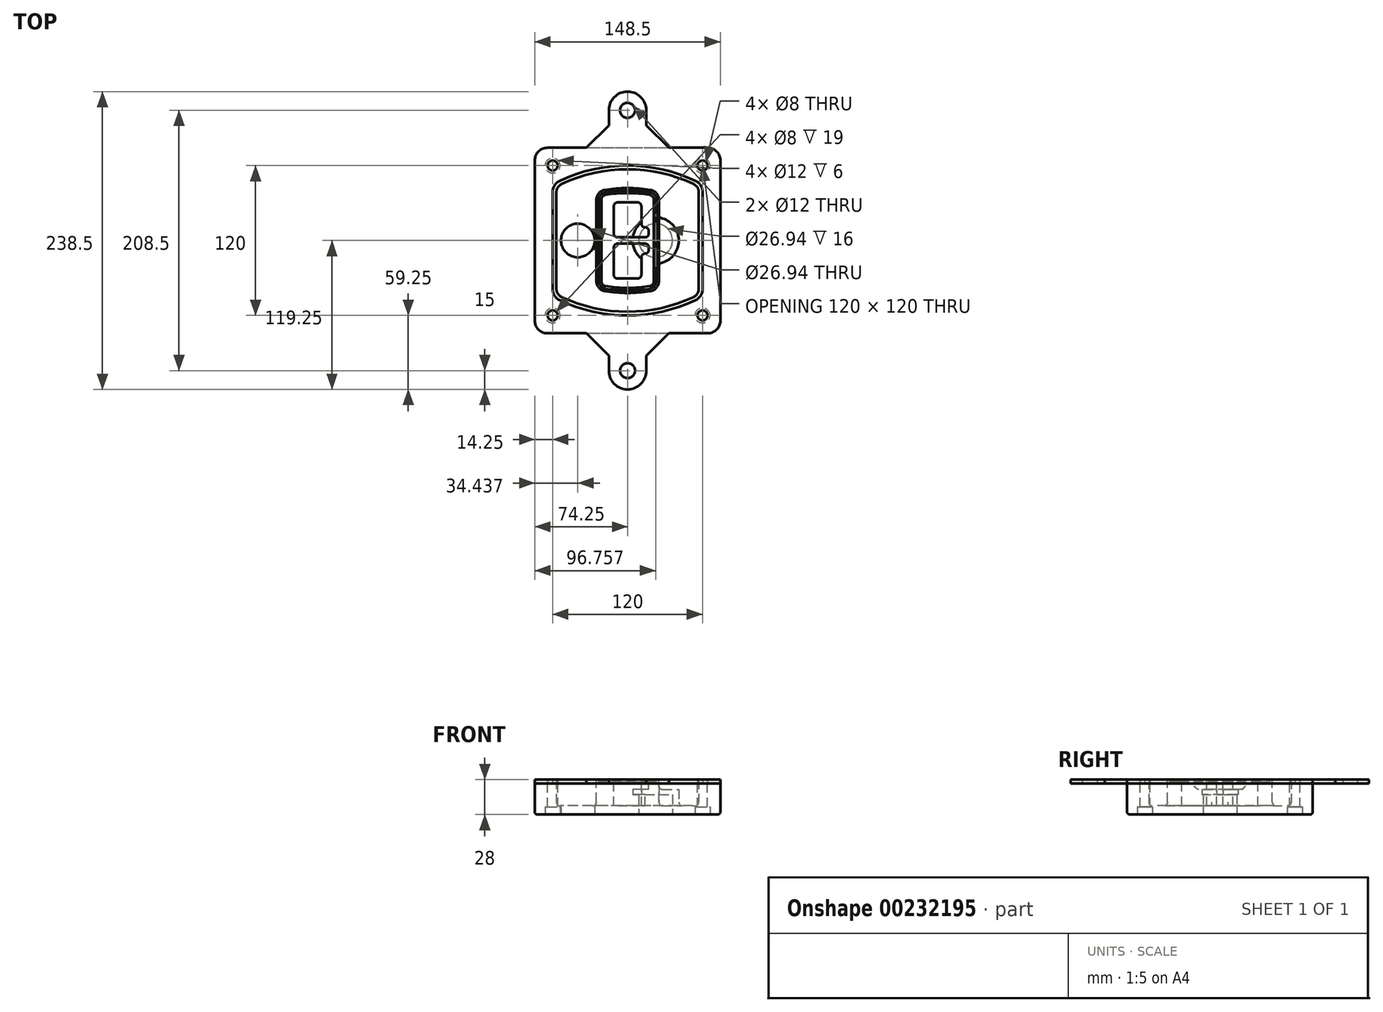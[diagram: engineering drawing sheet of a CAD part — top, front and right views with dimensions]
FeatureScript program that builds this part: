
annotation { "Feature Type Name" : "Feature", "Feature Type Description" : "" }
export const myFeature = defineFeature(function(context is Context, id is Id, definition is map)
    precondition{}
    {
        {
            var Q0;
            Q0=qCreatedBy(makeId("Top.planeOp"),FACE);
            var sketch = newSketch(context, id + "F0", { "sketchPlane" : qUnion([Q0])});
            skPoint(sketch, "E0.rect.middle", {"position": v(0, 0) * mm});
            skLineSegment(sketch, "E1.bottom", {"start": v(-64.25, -74.25) * mm, "end": v(64.25, -74.25) * mm});
            skLineSegment(sketch, "E1.top", {"start": v(-64.25, 74.25) * mm, "end": v(64.25, 74.25) * mm});
            skLineSegment(sketch, "E1.left", {"start": v(-74.25, -64.25) * mm, "end": v(-74.25, 64.25) * mm});
            skLineSegment(sketch, "E1.right", {"start": v(74.25, -64.25) * mm, "end": v(74.25, 64.25) * mm});
            skLineSegment(sketch, "E2", {"start": v(-74.25, 74.25) * mm, "end": v(74.25, -74.25) * mm, "construction": true});
            skLineSegment(sketch, "E3", {"start": v(74.25, 74.25) * mm, "end": v(-74.25, -74.25) * mm, "construction": true});
            skCircle(sketch, "E4", {"center": v(-60, 60) * mm, "radius": 4 * mm});
            skCircle(sketch, "E5", {"center": v(60, 60) * mm, "radius": 4 * mm});
            skCircle(sketch, "E6", {"center": v(60, -60) * mm, "radius": 4 * mm});
            skCircle(sketch, "E7", {"center": v(-60, -60) * mm, "radius": 4 * mm});
            skLineSegment(sketch, "E8", {"start": v(-60, 60) * mm, "end": v(60, 60) * mm, "construction": true});
            skLineSegment(sketch, "E9", {"start": v(60, 60) * mm, "end": v(60, -60) * mm, "construction": true});
            skLineSegment(sketch, "E10", {"start": v(60, -60) * mm, "end": v(-60, -60) * mm, "construction": true});
            skLineSegment(sketch, "E11", {"start": v(-60, -60) * mm, "end": v(-60, 60) * mm, "construction": true});
            skLineSegment(sketch, "E12", {"start": v(-60, 38.83) * mm, "end": v(-60, -38.83) * mm});
            skLineSegment(sketch, "E13", {"start": v(60, 38.83) * mm, "end": v(60, -38.83) * mm});
            skArc(sketch, "E14", {"start": v(54.26, 47.88) * mm, "mid": v(0, 60) * mm, "end": v(-54.26, 47.88) * mm});
            skArc(sketch, "E15", {"start": v(-54.26, -47.88) * mm, "mid": v(0, -60) * mm, "end": v(54.26, -47.88) * mm});
            skLineSegment(sketch, "E16", {"start": v(-60, 0) * mm, "end": v(60, 0) * mm, "construction": true});
            skPoint(sketch, "E17.visualSharp", {"position": v(-60, -45) * mm});
            skArc(sketch, "E17.filletArc", {"start": v(-60, -38.83) * mm, "mid": v(-58.44, -44.2) * mm, "end": v(-54.26, -47.88) * mm});
            skPoint(sketch, "E18.visualSharp", {"position": v(-60, 45) * mm});
            skArc(sketch, "E18.filletArc", {"start": v(-54.26, 47.88) * mm, "mid": v(-58.44, 44.2) * mm, "end": v(-60, 38.83) * mm});
            skPoint(sketch, "E19.visualSharp", {"position": v(60, 45) * mm});
            skArc(sketch, "E19.filletArc", {"start": v(60, 38.83) * mm, "mid": v(58.44, 44.2) * mm, "end": v(54.26, 47.88) * mm});
            skPoint(sketch, "E20.visualSharp", {"position": v(60, -45) * mm});
            skArc(sketch, "E20.filletArc", {"start": v(54.26, -47.88) * mm, "mid": v(58.44, -44.2) * mm, "end": v(60, -38.83) * mm});
            skPoint(sketch, "E21.visualSharp", {"position": v(-74.25, 74.25) * mm});
            skArc(sketch, "E21.filletArc", {"start": v(-64.25, 74.25) * mm, "mid": v(-71.32, 71.32) * mm, "end": v(-74.25, 64.25) * mm});
            skPoint(sketch, "E22.visualSharp", {"position": v(74.25, 74.25) * mm});
            skArc(sketch, "E22.filletArc", {"start": v(74.25, 64.25) * mm, "mid": v(71.32, 71.32) * mm, "end": v(64.25, 74.25) * mm});
            skPoint(sketch, "E23.visualSharp", {"position": v(74.25, -74.25) * mm});
            skArc(sketch, "E23.filletArc", {"start": v(64.25, -74.25) * mm, "mid": v(71.32, -71.32) * mm, "end": v(74.25, -64.25) * mm});
            skPoint(sketch, "E24.visualSharp", {"position": v(-74.25, -74.25) * mm});
            skArc(sketch, "E24.filletArc", {"start": v(-74.25, -64.25) * mm, "mid": v(-71.32, -71.32) * mm, "end": v(-64.25, -74.25) * mm});
            skArc(sketch, "E25.0", {"start": v(57, 38.83) * mm, "mid": v(55.9, 42.58) * mm, "end": v(52.98, 45.17) * mm});
            skLineSegment(sketch, "E25.1", {"start": v(57, 38.83) * mm, "end": v(57, -38.83) * mm});
            skArc(sketch, "E25.2", {"start": v(52.98, -45.17) * mm, "mid": v(55.9, -42.58) * mm, "end": v(57, -38.83) * mm});
            skArc(sketch, "E25.3", {"start": v(-52.98, -45.17) * mm, "mid": v(0, -57) * mm, "end": v(52.98, -45.17) * mm});
            skArc(sketch, "E25.4", {"start": v(-57, -38.83) * mm, "mid": v(-55.9, -42.58) * mm, "end": v(-52.98, -45.17) * mm});
            skArc(sketch, "E25.5", {"start": v(52.98, 45.17) * mm, "mid": v(0, 57) * mm, "end": v(-52.98, 45.17) * mm});
            skLineSegment(sketch, "E25.6", {"start": v(-57, 38.83) * mm, "end": v(-57, -38.83) * mm});
            skArc(sketch, "E25.7", {"start": v(-52.98, 45.17) * mm, "mid": v(-55.9, 42.58) * mm, "end": v(-57, 38.83) * mm});
            skArc(sketch, "E26.0", {"start": v(-55.96, 51.5) * mm, "mid": v(-61.82, 46.33) * mm, "end": v(-64, 38.83) * mm});
            skArc(sketch, "E26.1", {"start": v(55.96, 51.5) * mm, "mid": v(0, 64) * mm, "end": v(-55.96, 51.5) * mm});
            skArc(sketch, "E26.2", {"start": v(64, 38.83) * mm, "mid": v(61.82, 46.33) * mm, "end": v(55.96, 51.5) * mm});
            skLineSegment(sketch, "E26.3", {"start": v(64, 38.83) * mm, "end": v(64, -38.83) * mm});
            skArc(sketch, "E26.4", {"start": v(55.96, -51.5) * mm, "mid": v(61.82, -46.33) * mm, "end": v(64, -38.83) * mm});
            skLineSegment(sketch, "E26.5", {"start": v(-64, 38.83) * mm, "end": v(-64, -38.83) * mm});
            skArc(sketch, "E26.6", {"start": v(-55.96, -51.5) * mm, "mid": v(0, -64) * mm, "end": v(55.96, -51.5) * mm});
            skArc(sketch, "E26.7", {"start": v(-64, -38.83) * mm, "mid": v(-61.82, -46.33) * mm, "end": v(-55.96, -51.5) * mm});
            skSolve(sketch);
        }
        {
            var Q0;
            Q0=makeQuery(id+"F0.imprint","IMPRINT",FACE,{"disambiguationData":[TD([[makeQuery(id+"F0.imprint","IMPRINT",EDGE,{"derivedFrom":sQuery(id+"F0.wireOp",EDGE,"E1.bottom")}),1.0]])]});
            var Q1;
            Q1=makeQuery(id+"F0.imprint","IMPRINT",FACE,{"disambiguationData":[TD([[makeQuery(id+"F0.imprint","IMPRINT",EDGE,{"derivedFrom":sQuery(id+"F0.wireOp",EDGE,"E12")}),1.0]])]});
            var Q2;
            Q2=makeQuery(id+"F0.imprint","IMPRINT",FACE,{"disambiguationData":[TD([[makeQuery(id+"F0.imprint","IMPRINT",EDGE,{"derivedFrom":sQuery(id+"F0.wireOp",EDGE,"E25.0")}),1.0]])]});
            var Q3;
            Q3=makeQuery(id+"F0.imprint","IMPRINT",FACE,{"disambiguationData":[TD([[makeQuery(id+"F0.imprint","IMPRINT",EDGE,{"derivedFrom":sQuery(id+"F0.wireOp",EDGE,"E12")}),-1.0]])]});
            extrude(context, id + "F1", {"entities" : qUnion([Q0, Q1, Q2, Q3]), "oppositeDirection" : true, "depth" : 25 * mm});
        }
        {
            var Q0;
            Q0=makeQuery(id+"F0.imprint","IMPRINT",FACE,{"disambiguationData":[TD([[makeQuery(id+"F0.imprint","IMPRINT",EDGE,{"derivedFrom":sQuery(id+"F0.wireOp",EDGE,"E12")}),1.0]])]});
            extrude(context, id + "F2", {"entities" : qUnion([Q0]), "operationType" : NewBodyOperationType.ADD, "depth" : 3 * mm});
        }
        {
            var Q0;
            Q0=makeQuery(id+"F0.imprint","IMPRINT",FACE,{"disambiguationData":[TD([[makeQuery(id+"F0.imprint","IMPRINT",EDGE,{"derivedFrom":sQuery(id+"F0.wireOp",EDGE,"E25.0")}),1.0]])]});
            extrude(context, id + "F3", {"entities" : qUnion([Q0]), "operationType" : NewBodyOperationType.REMOVE, "oppositeDirection" : true, "depth" : 18 * mm});
        }
        {
            var Q0;
            Q0=makeQuery(id+"F2.opExtrude","CAP_FACE",FACE,{"disambiguationData":[OSD([sQuery(id+"F0.wireOp",EDGE,"E12"),sQuery(id+"F0.wireOp",EDGE,"E13"),sQuery(id+"F0.wireOp",EDGE,"E14"),sQuery(id+"F0.wireOp",EDGE,"E15"),sQuery(id+"F0.wireOp",EDGE,"E17.filletArc"),sQuery(id+"F0.wireOp",EDGE,"E18.filletArc"),sQuery(id+"F0.wireOp",EDGE,"E19.filletArc"),sQuery(id+"F0.wireOp",EDGE,"E20.filletArc"),sQuery(id+"F0.wireOp",EDGE,"E25.0"),sQuery(id+"F0.wireOp",EDGE,"E25.1"),sQuery(id+"F0.wireOp",EDGE,"E25.2"),sQuery(id+"F0.wireOp",EDGE,"E25.3"),sQuery(id+"F0.wireOp",EDGE,"E25.4"),sQuery(id+"F0.wireOp",EDGE,"E25.5"),sQuery(id+"F0.wireOp",EDGE,"E25.6"),sQuery(id+"F0.wireOp",EDGE,"E25.7")])],"isStart":false});
            var sketch = newSketch(context, id + "F4", { "sketchPlane" : qUnion([Q0])});
            skArc(sketch, "E27.0", {"start": v(-18.34, -40.45) * mm, "mid": v(0, -42) * mm, "end": v(18.34, -40.45) * mm});
            skArc(sketch, "E28.0", {"start": v(18.34, 40.45) * mm, "mid": v(0, 42) * mm, "end": v(-18.34, 40.45) * mm});
            skLineSegment(sketch, "E29", {"start": v(-25, 32.57) * mm, "end": v(-25, -32.57) * mm});
            skLineSegment(sketch, "E30", {"start": v(25, 32.57) * mm, "end": v(25, -32.57) * mm});
            skLineSegment(sketch, "E31", {"start": v(-25, 39.1) * mm, "end": v(25, 39.1) * mm, "construction": true});
            skLineSegment(sketch, "E32", {"start": v(-25, -39.1) * mm, "end": v(25, -39.1) * mm, "construction": true});
            skPoint(sketch, "E33.visualSharp", {"position": v(-25, 39.1) * mm});
            skArc(sketch, "E33.filletArc", {"start": v(-18.34, 40.45) * mm, "mid": v(-23.11, 37.73) * mm, "end": v(-25, 32.57) * mm});
            skPoint(sketch, "E34.visualSharp", {"position": v(25, 39.1) * mm});
            skArc(sketch, "E34.filletArc", {"start": v(25, 32.57) * mm, "mid": v(23.11, 37.73) * mm, "end": v(18.34, 40.45) * mm});
            skPoint(sketch, "E35.visualSharp", {"position": v(25, -39.1) * mm});
            skArc(sketch, "E35.filletArc", {"start": v(18.34, -40.45) * mm, "mid": v(23.11, -37.73) * mm, "end": v(25, -32.57) * mm});
            skPoint(sketch, "E36.visualSharp", {"position": v(-25, -39.1) * mm});
            skArc(sketch, "E36.filletArc", {"start": v(-25, -32.57) * mm, "mid": v(-23.11, -37.73) * mm, "end": v(-18.34, -40.45) * mm});
            skArc(sketch, "E37.0", {"start": v(52.98, 45.17) * mm, "mid": v(0, 57) * mm, "end": v(-52.98, 45.17) * mm});
            skArc(sketch, "E37.1", {"start": v(-52.98, 45.17) * mm, "mid": v(-55.9, 42.58) * mm, "end": v(-57, 38.83) * mm});
            skLineSegment(sketch, "E37.2", {"start": v(-57, 38.83) * mm, "end": v(-57, -38.83) * mm});
            skArc(sketch, "E37.3", {"start": v(-57, -38.83) * mm, "mid": v(-55.9, -42.58) * mm, "end": v(-52.98, -45.17) * mm});
            skArc(sketch, "E37.4", {"start": v(-52.98, -45.17) * mm, "mid": v(0, -57) * mm, "end": v(52.98, -45.17) * mm});
            skArc(sketch, "E37.5", {"start": v(52.98, -45.17) * mm, "mid": v(55.9, -42.58) * mm, "end": v(57, -38.83) * mm});
            skLineSegment(sketch, "E37.6", {"start": v(57, 38.83) * mm, "end": v(57, -38.83) * mm});
            skArc(sketch, "E37.7", {"start": v(57, 38.83) * mm, "mid": v(55.9, 42.58) * mm, "end": v(52.98, 45.17) * mm});
            skLineSegment(sketch, "E38.0", {"start": v(23, 32.57) * mm, "end": v(23, -32.57) * mm});
            skArc(sketch, "E38.1", {"start": v(18, -38.48) * mm, "mid": v(21.58, -36.44) * mm, "end": v(23, -32.57) * mm});
            skArc(sketch, "E38.2", {"start": v(-18, -38.48) * mm, "mid": v(0, -40) * mm, "end": v(18, -38.48) * mm});
            skArc(sketch, "E38.3", {"start": v(-23, -32.57) * mm, "mid": v(-21.58, -36.44) * mm, "end": v(-18, -38.48) * mm});
            skLineSegment(sketch, "E38.4", {"start": v(-23, 32.57) * mm, "end": v(-23, -32.57) * mm});
            skArc(sketch, "E38.5", {"start": v(23, 32.57) * mm, "mid": v(21.58, 36.44) * mm, "end": v(18, 38.48) * mm});
            skArc(sketch, "E38.6", {"start": v(-18, 38.48) * mm, "mid": v(-21.58, 36.44) * mm, "end": v(-23, 32.57) * mm});
            skArc(sketch, "E38.7", {"start": v(18, 38.48) * mm, "mid": v(0, 40) * mm, "end": v(-18, 38.48) * mm});
            skArc(sketch, "E39.0", {"start": v(21, 32.57) * mm, "mid": v(20.06, 35.15) * mm, "end": v(17.67, 36.5) * mm});
            skLineSegment(sketch, "E39.1", {"start": v(21, 32.57) * mm, "end": v(21, -32.57) * mm});
            skArc(sketch, "E39.2", {"start": v(17.67, -36.5) * mm, "mid": v(20.06, -35.15) * mm, "end": v(21, -32.57) * mm});
            skArc(sketch, "E39.3", {"start": v(-17.67, -36.5) * mm, "mid": v(0, -38) * mm, "end": v(17.67, -36.5) * mm});
            skArc(sketch, "E39.4", {"start": v(-21, -32.57) * mm, "mid": v(-20.06, -35.15) * mm, "end": v(-17.67, -36.5) * mm});
            skArc(sketch, "E39.5", {"start": v(17.67, 36.5) * mm, "mid": v(0, 38) * mm, "end": v(-17.67, 36.5) * mm});
            skLineSegment(sketch, "E39.6", {"start": v(-21, 32.57) * mm, "end": v(-21, -32.57) * mm});
            skArc(sketch, "E39.7", {"start": v(-17.67, 36.5) * mm, "mid": v(-20.06, 35.15) * mm, "end": v(-21, 32.57) * mm});
            skLineSegment(sketch, "E40", {"start": v(-25, 0) * mm, "end": v(25, 0) * mm, "construction": true});
            skLineSegment(sketch, "E41", {"start": v(-11, 5.5) * mm, "end": v(-11, 27.5) * mm});
            skLineSegment(sketch, "E42", {"start": v(-8, 30.5) * mm, "end": v(8, 30.5) * mm});
            skLineSegment(sketch, "E43", {"start": v(11, 27.5) * mm, "end": v(11, 13.5) * mm});
            skLineSegment(sketch, "E44", {"start": v(14, 10.5) * mm, "end": v(14, 10.5) * mm});
            skLineSegment(sketch, "E45", {"start": v(17, 7.5) * mm, "end": v(17, 5.5) * mm});
            skLineSegment(sketch, "E46", {"start": v(14, 2.5) * mm, "end": v(-8, 2.5) * mm});
            skPoint(sketch, "E47.visualSharp", {"position": v(-11, 30.5) * mm});
            skArc(sketch, "E47.filletArc", {"start": v(-8, 30.5) * mm, "mid": v(-10.12, 29.62) * mm, "end": v(-11, 27.5) * mm});
            skPoint(sketch, "E48.visualSharp", {"position": v(11, 30.5) * mm});
            skArc(sketch, "E48.filletArc", {"start": v(11, 27.5) * mm, "mid": v(10.12, 29.62) * mm, "end": v(8, 30.5) * mm});
            skPoint(sketch, "E49.visualSharp", {"position": v(11, 10.5) * mm});
            skArc(sketch, "E49.filletArc", {"start": v(11, 13.5) * mm, "mid": v(11.88, 11.38) * mm, "end": v(14, 10.5) * mm});
            skPoint(sketch, "E50.visualSharp", {"position": v(17, 10.5) * mm});
            skArc(sketch, "E50.filletArc", {"start": v(17, 7.5) * mm, "mid": v(16.12, 9.62) * mm, "end": v(14, 10.5) * mm});
            skPoint(sketch, "E51.visualSharp", {"position": v(17, 2.5) * mm});
            skArc(sketch, "E51.filletArc", {"start": v(14, 2.5) * mm, "mid": v(16.12, 3.38) * mm, "end": v(17, 5.5) * mm});
            skPoint(sketch, "E52.visualSharp", {"position": v(-11, 2.5) * mm});
            skArc(sketch, "E52.filletArc", {"start": v(-11, 5.5) * mm, "mid": v(-10.12, 3.38) * mm, "end": v(-8, 2.5) * mm});
            skLineSegment(sketch, "E53.0.MirrorCS", {"start": v(14, -2.5) * mm, "end": v(-8, -2.5) * mm});
            skArc(sketch, "E54.0.MirrorCS", {"start": v(-11, -5.5) * mm, "mid": v(-10.12, -3.38) * mm, "end": v(-8, -2.5) * mm});
            skLineSegment(sketch, "E55.0.MirrorCS", {"start": v(-11, -5.5) * mm, "end": v(-11, -27.5) * mm});
            skArc(sketch, "E56.0.MirrorCS", {"start": v(-8, -30.5) * mm, "mid": v(-10.12, -29.62) * mm, "end": v(-11, -27.5) * mm});
            skLineSegment(sketch, "E57.0.MirrorCS", {"start": v(-8, -30.5) * mm, "end": v(8, -30.5) * mm});
            skArc(sketch, "E58.0.MirrorCS", {"start": v(11, -27.5) * mm, "mid": v(10.12, -29.62) * mm, "end": v(8, -30.5) * mm});
            skLineSegment(sketch, "E59.0.MirrorCS", {"start": v(11, -27.5) * mm, "end": v(11, -13.5) * mm});
            skArc(sketch, "E60.0.MirrorCS", {"start": v(11, -13.5) * mm, "mid": v(11.88, -11.38) * mm, "end": v(14, -10.5) * mm});
            skArc(sketch, "E61.0.MirrorCS", {"start": v(17, -7.5) * mm, "mid": v(16.12, -9.62) * mm, "end": v(14, -10.5) * mm});
            skLineSegment(sketch, "E62.0.MirrorCS", {"start": v(17, -7.5) * mm, "end": v(17, -5.5) * mm});
            skArc(sketch, "E63.0.MirrorCS", {"start": v(14, -2.5) * mm, "mid": v(16.12, -3.38) * mm, "end": v(17, -5.5) * mm});
            skSolve(sketch);
        }
        {
            var Q0;
            Q0=makeQuery(id+"F4.imprint","IMPRINT",FACE,{"disambiguationData":[TD([[makeQuery(id+"F4.imprint","IMPRINT",EDGE,{"derivedFrom":sQuery(id+"F4.wireOp",EDGE,"E27.0")}),1.0]])]});
            var Q1;
            Q1=makeQuery(id+"F4.imprint","IMPRINT",FACE,{"disambiguationData":[TD([[makeQuery(id+"F4.imprint","IMPRINT",EDGE,{"derivedFrom":sQuery(id+"F4.wireOp",EDGE,"E38.0")}),-1.0]])]});
            var Q2;
            Q2=makeQuery(id+"F4.imprint","IMPRINT",FACE,{"disambiguationData":[TD([[makeQuery(id+"F4.imprint","IMPRINT",EDGE,{"derivedFrom":sQuery(id+"F4.wireOp",EDGE,"E39.0")}),1.0]])]});
            extrude(context, id + "F5", {"entities" : qUnion([Q0, Q1, Q2]), "operationType" : NewBodyOperationType.ADD, "endBound" : BoundingType.UP_TO_NEXT, "oppositeDirection" : true, "depth" : 25 * mm});
        }
        {
            var Q0;
            Q0=makeQuery(id+"F4.imprint","IMPRINT",FACE,{"disambiguationData":[TD([[makeQuery(id+"F4.imprint","IMPRINT",EDGE,{"derivedFrom":sQuery(id+"F4.wireOp",EDGE,"E38.0")}),-1.0]])]});
            extrude(context, id + "F6", {"entities" : qUnion([Q0]), "operationType" : NewBodyOperationType.REMOVE, "oppositeDirection" : true, "depth" : 2 * mm});
        }
        {
            var Q0;
            Q0=makeQuery(id+"F1.opExtrude","CAP_FACE",FACE,{"disambiguationData":[OSD([sQuery(id+"F0.wireOp",EDGE,"E1.bottom"),sQuery(id+"F0.wireOp",EDGE,"E1.top"),sQuery(id+"F0.wireOp",EDGE,"E1.left"),sQuery(id+"F0.wireOp",EDGE,"E1.right"),sQuery(id+"F0.wireOp",EDGE,"E4"),sQuery(id+"F0.wireOp",EDGE,"E5"),sQuery(id+"F0.wireOp",EDGE,"E6"),sQuery(id+"F0.wireOp",EDGE,"E7"),sQuery(id+"F0.wireOp",EDGE,"E21.filletArc"),sQuery(id+"F0.wireOp",EDGE,"E22.filletArc"),sQuery(id+"F0.wireOp",EDGE,"E23.filletArc"),sQuery(id+"F0.wireOp",EDGE,"E24.filletArc")])],"isStart":false});
            var sketch = newSketch(context, id + "F7", { "sketchPlane" : qUnion([Q0])});
            skCircle(sketch, "E64", {"center": v(22.5, 0) * mm, "radius": 13.47 * mm});
            skCircle(sketch, "E65", {"center": v(-39.81, 0) * mm, "radius": 13.47 * mm});
            skLineSegment(sketch, "E66", {"start": v(74.25, 0) * mm, "end": v(-74.25, 0) * mm});
            skCircle(sketch, "E67", {"center": v(22.5, 0) * mm, "radius": 18.47 * mm});
            skCircle(sketch, "E68", {"center": v(60, -60) * mm, "radius": 6 * mm});
            skCircle(sketch, "E69", {"center": v(-60, -60) * mm, "radius": 6 * mm});
            skCircle(sketch, "E70", {"center": v(-60, 60) * mm, "radius": 6 * mm});
            skCircle(sketch, "E71", {"center": v(60, 60) * mm, "radius": 6 * mm});
            skSolve(sketch);
        }
        {
            var Q0;
            {var subQ1=sQuery(id+"F7.wireOp",EDGE,"E66");var subQ4=sQuery(id+"F7.wireOp",EDGE,"E64");var subQ6=makeQuery(id+"F7.imprint","INTERSECT",VERTEX,{"disambiguationData":[OD(0.0)],"derivedFrom":[subQ4,subQ1]});Q0=makeQuery(id+"F7.imprint","IMPRINT",FACE,{"disambiguationData":[TD([[makeQuery(id+"F7.imprint","IMPRINT",EDGE,{"disambiguationData":[TD([[subQ6,-1.0]])],"derivedFrom":subQ4}),-1.0]])]});}
            var Q1;
            {var subQ0=sQuery(id+"F7.wireOp",EDGE,"E66");var subQ1=sQuery(id+"F7.wireOp",EDGE,"E64");var subQ3=makeQuery(id+"F7.imprint","INTERSECT",VERTEX,{"disambiguationData":[OD(0.0)],"derivedFrom":[subQ1,subQ0]});Q1=makeQuery(id+"F7.imprint","IMPRINT",FACE,{"disambiguationData":[TD([[makeQuery(id+"F7.imprint","IMPRINT",EDGE,{"disambiguationData":[TD([[subQ3,-1.0]])],"derivedFrom":subQ1}),1.0]])]});}
            var Q2;
            {var subQ0=sQuery(id+"F7.wireOp",EDGE,"E66");var subQ1=sQuery(id+"F7.wireOp",EDGE,"E64");var subQ3=makeQuery(id+"F7.imprint","INTERSECT",VERTEX,{"disambiguationData":[OD(0.0)],"derivedFrom":[subQ1,subQ0]});Q2=makeQuery(id+"F7.imprint","IMPRINT",FACE,{"disambiguationData":[TD([[makeQuery(id+"F7.imprint","IMPRINT",EDGE,{"disambiguationData":[TD([[subQ3,1.0]])],"derivedFrom":subQ1}),1.0]])]});}
            var Q3;
            {var subQ1=sQuery(id+"F7.wireOp",EDGE,"E66");var subQ4=sQuery(id+"F7.wireOp",EDGE,"E64");var subQ6=makeQuery(id+"F7.imprint","INTERSECT",VERTEX,{"disambiguationData":[OD(0.0)],"derivedFrom":[subQ4,subQ1]});Q3=makeQuery(id+"F7.imprint","IMPRINT",FACE,{"disambiguationData":[TD([[makeQuery(id+"F7.imprint","IMPRINT",EDGE,{"disambiguationData":[TD([[subQ6,1.0]])],"derivedFrom":subQ4}),-1.0]])]});}
            extrude(context, id + "F8", {"entities" : qUnion([Q0, Q1, Q2, Q3]), "operationType" : NewBodyOperationType.ADD, "oppositeDirection" : true, "depth" : 20 * mm});
        }
        {
            var Q0;
            {var subQ0=sQuery(id+"F7.wireOp",EDGE,"E66");var subQ1=sQuery(id+"F7.wireOp",EDGE,"E64");var subQ3=makeQuery(id+"F7.imprint","INTERSECT",VERTEX,{"disambiguationData":[OD(0.0)],"derivedFrom":[subQ1,subQ0]});Q0=makeQuery(id+"F7.imprint","IMPRINT",FACE,{"disambiguationData":[TD([[makeQuery(id+"F7.imprint","IMPRINT",EDGE,{"disambiguationData":[TD([[subQ3,-1.0]])],"derivedFrom":subQ1}),1.0]])]});}
            var Q1;
            {var subQ0=sQuery(id+"F7.wireOp",EDGE,"E66");var subQ1=sQuery(id+"F7.wireOp",EDGE,"E64");var subQ3=makeQuery(id+"F7.imprint","INTERSECT",VERTEX,{"disambiguationData":[OD(0.0)],"derivedFrom":[subQ1,subQ0]});Q1=makeQuery(id+"F7.imprint","IMPRINT",FACE,{"disambiguationData":[TD([[makeQuery(id+"F7.imprint","IMPRINT",EDGE,{"disambiguationData":[TD([[subQ3,1.0]])],"derivedFrom":subQ1}),1.0]])]});}
            extrude(context, id + "F9", {"entities" : qUnion([Q0, Q1]), "operationType" : NewBodyOperationType.REMOVE, "oppositeDirection" : true, "depth" : 16 * mm});
        }
        {
            var Q0;
            {var subQ0=sQuery(id+"F7.wireOp",EDGE,"E66");var subQ1=sQuery(id+"F7.wireOp",EDGE,"E65");var subQ3=makeQuery(id+"F7.imprint","INTERSECT",VERTEX,{"disambiguationData":[OD(0.0)],"derivedFrom":[subQ1,subQ0]});Q0=makeQuery(id+"F7.imprint","IMPRINT",FACE,{"disambiguationData":[TD([[makeQuery(id+"F7.imprint","IMPRINT",EDGE,{"disambiguationData":[TD([[subQ3,-1.0]])],"derivedFrom":subQ1}),1.0]])]});}
            var Q1;
            {var subQ0=sQuery(id+"F7.wireOp",EDGE,"E66");var subQ1=sQuery(id+"F7.wireOp",EDGE,"E65");var subQ3=makeQuery(id+"F7.imprint","INTERSECT",VERTEX,{"disambiguationData":[OD(0.0)],"derivedFrom":[subQ1,subQ0]});Q1=makeQuery(id+"F7.imprint","IMPRINT",FACE,{"disambiguationData":[TD([[makeQuery(id+"F7.imprint","IMPRINT",EDGE,{"disambiguationData":[TD([[subQ3,1.0]])],"derivedFrom":subQ1}),1.0]])]});}
            extrude(context, id + "F10", {"entities" : qUnion([Q0, Q1]), "operationType" : NewBodyOperationType.REMOVE, "oppositeDirection" : true, "depth" : 25 * mm});
        }
        {
            var Q0;
            Q0=makeQuery(id+"F7.imprint","IMPRINT",FACE,{"disambiguationData":[TD([[makeQuery(id+"F7.imprint","IMPRINT",EDGE,{"derivedFrom":sQuery(id+"F7.wireOp",EDGE,"E68")}),1.0]])]});
            var Q1;
            Q1=makeQuery(id+"F7.imprint","IMPRINT",FACE,{"disambiguationData":[TD([[makeQuery(id+"F7.imprint","IMPRINT",EDGE,{"derivedFrom":makeQuery(id+"F1.opExtrude","CAP_EDGE",EDGE,{"disambiguationData":[OSD([sQuery(id+"F0.wireOp",EDGE,"E5")])],"isStart":false})}),-1.0]])]});
            var Q2;
            Q2=makeQuery(id+"F7.imprint","IMPRINT",FACE,{"disambiguationData":[TD([[makeQuery(id+"F7.imprint","IMPRINT",EDGE,{"derivedFrom":sQuery(id+"F7.wireOp",EDGE,"E69")}),1.0]])]});
            var Q3;
            Q3=makeQuery(id+"F7.imprint","IMPRINT",FACE,{"disambiguationData":[TD([[makeQuery(id+"F7.imprint","IMPRINT",EDGE,{"derivedFrom":makeQuery(id+"F1.opExtrude","CAP_EDGE",EDGE,{"disambiguationData":[OSD([sQuery(id+"F0.wireOp",EDGE,"E4")])],"isStart":false})}),-1.0]])]});
            var Q4;
            Q4=makeQuery(id+"F7.imprint","IMPRINT",FACE,{"disambiguationData":[TD([[makeQuery(id+"F7.imprint","IMPRINT",EDGE,{"derivedFrom":sQuery(id+"F7.wireOp",EDGE,"E70")}),1.0]])]});
            var Q5;
            Q5=makeQuery(id+"F7.imprint","IMPRINT",FACE,{"disambiguationData":[TD([[makeQuery(id+"F7.imprint","IMPRINT",EDGE,{"derivedFrom":makeQuery(id+"F1.opExtrude","CAP_EDGE",EDGE,{"disambiguationData":[OSD([sQuery(id+"F0.wireOp",EDGE,"E7")])],"isStart":false})}),-1.0]])]});
            var Q6;
            Q6=makeQuery(id+"F7.imprint","IMPRINT",FACE,{"disambiguationData":[TD([[makeQuery(id+"F7.imprint","IMPRINT",EDGE,{"derivedFrom":sQuery(id+"F7.wireOp",EDGE,"E71")}),1.0]])]});
            var Q7;
            Q7=makeQuery(id+"F7.imprint","IMPRINT",FACE,{"disambiguationData":[TD([[makeQuery(id+"F7.imprint","IMPRINT",EDGE,{"derivedFrom":makeQuery(id+"F1.opExtrude","CAP_EDGE",EDGE,{"disambiguationData":[OSD([sQuery(id+"F0.wireOp",EDGE,"E6")])],"isStart":false})}),-1.0]])]});
            extrude(context, id + "F11", {"entities" : qUnion([Q0, Q1, Q2, Q3, Q4, Q5, Q6, Q7]), "operationType" : NewBodyOperationType.REMOVE, "oppositeDirection" : true, "depth" : 6 * mm});
        }
        {
            var Q0;
            Q0=makeQuery(id+"F9.boolean.opBoolean","COPY",FACE,{"derivedFrom":makeQuery(id+"F9.opExtrude","CAP_FACE",FACE,{"disambiguationData":[OSD([sQuery(id+"F7.wireOp",EDGE,"E64")])],"isStart":false})});
            var sketch = newSketch(context, id + "F12", { "sketchPlane" : qUnion([Q0])});
            skArc(sketch, "E72.0", {"start": v(11, 14.45) * mm, "mid": v(6.45, 9.13) * mm, "end": v(4.2, 2.5) * mm});
            skArc(sketch, "E72.1", {"start": v(4.2, -2.5) * mm, "mid": v(6.45, -9.13) * mm, "end": v(11, -14.45) * mm});
            skLineSegment(sketch, "E73", {"start": v(4.2, -2.5) * mm, "end": v(14, -2.5) * mm});
            skLineSegment(sketch, "E74.0", {"start": v(14, 2.5) * mm, "end": v(4.2, 2.5) * mm});
            skArc(sketch, "E74.1", {"start": v(14, 2.5) * mm, "mid": v(16.12, 3.38) * mm, "end": v(17, 5.5) * mm});
            skLineSegment(sketch, "E74.2", {"start": v(17, 7.5) * mm, "end": v(17, 5.5) * mm});
            skArc(sketch, "E74.3", {"start": v(17, 7.5) * mm, "mid": v(16.12, 9.62) * mm, "end": v(14, 10.5) * mm});
            skArc(sketch, "E74.4", {"start": v(11, 13.5) * mm, "mid": v(11.88, 11.38) * mm, "end": v(14, 10.5) * mm});
            skLineSegment(sketch, "E74.5", {"start": v(11, 14.45) * mm, "end": v(11, 13.5) * mm});
            skLineSegment(sketch, "E74.7", {"start": v(14, -2.5) * mm, "end": v(4.2, -2.5) * mm});
            skArc(sketch, "E74.8", {"start": v(14, -2.5) * mm, "mid": v(16.12, -3.38) * mm, "end": v(17, -5.5) * mm});
            skLineSegment(sketch, "E74.9", {"start": v(17, -7.5) * mm, "end": v(17, -5.5) * mm});
            skArc(sketch, "E74.10", {"start": v(17, -7.5) * mm, "mid": v(16.12, -9.62) * mm, "end": v(14, -10.5) * mm});
            skArc(sketch, "E74.11", {"start": v(11, -13.5) * mm, "mid": v(11.88, -11.38) * mm, "end": v(14, -10.5) * mm});
            skLineSegment(sketch, "E74.12", {"start": v(11, -14.45) * mm, "end": v(11, -13.5) * mm});
            skPoint(sketch, "E75.orphan", {"position": v(11, -27.5) * mm});
            skPoint(sketch, "E76.orphan", {"position": v(-8, -2.5) * mm});
            skPoint(sketch, "E77.orphan", {"position": v(-8, 2.5) * mm});
            skPoint(sketch, "E78.orphan", {"position": v(11, 27.5) * mm});
            skSolve(sketch);
        }
        {
            var Q0;
            {var subQ7=sQuery(id+"F12.wireOp",EDGE,"E72.0");var subQ14=sQuery(id+"F12.wireOp",EDGE,"E72.1");var subQ16=sQuery(id+"F12.wireOp",EDGE,"E74.1");var subQ18=sQuery(id+"F12.wireOp",EDGE,"E74.8");Q0=qUnion([makeQuery(id+"F12.imprint","IMPRINT",FACE,{"disambiguationData":[TD([[makeQuery(id+"F12.imprint","IMPRINT",EDGE,{"derivedFrom":subQ7}),1.0]])]}),makeQuery(id+"F12.imprint","IMPRINT",FACE,{"disambiguationData":[TD([[makeQuery(id+"F12.imprint","IMPRINT",EDGE,{"derivedFrom":subQ14}),1.0]])]}),makeQuery(id+"F12.imprint","IMPRINT",FACE,{"disambiguationData":[TD([[makeQuery(id+"F12.imprint","IMPRINT",EDGE,{"derivedFrom":subQ16}),1.0]])]}),makeQuery(id+"F12.imprint","IMPRINT",FACE,{"disambiguationData":[TD([[makeQuery(id+"F12.imprint","IMPRINT",EDGE,{"derivedFrom":subQ18}),-1.0]])]})]);}
            var Q1;
            Q1=makeQuery(id+"F5.boolean.opBoolean","SPLIT",FACE,{"disambiguationData":[TD([makeQuery(id+"F5.opExtrude","SWEPT_FACE",FACE,{"disambiguationData":[OSD([sQuery(id+"F4.wireOp",EDGE,"E41")])]})])],"derivedFrom":makeQuery(id+"F3.boolean.opBoolean","COPY",FACE,{"derivedFrom":makeQuery(id+"F3.opExtrude","CAP_FACE",FACE,{"disambiguationData":[OSD([sQuery(id+"F0.wireOp",EDGE,"E25.0"),sQuery(id+"F0.wireOp",EDGE,"E25.1"),sQuery(id+"F0.wireOp",EDGE,"E25.2"),sQuery(id+"F0.wireOp",EDGE,"E25.3"),sQuery(id+"F0.wireOp",EDGE,"E25.4"),sQuery(id+"F0.wireOp",EDGE,"E25.5"),sQuery(id+"F0.wireOp",EDGE,"E25.6"),sQuery(id+"F0.wireOp",EDGE,"E25.7")])],"isStart":false})})});
            extrude(context, id + "F13", {"entities" : qUnion([Q0]), "operationType" : NewBodyOperationType.REMOVE, "endBound" : BoundingType.UP_TO_SURFACE, "endBoundEntityFace" : qUnion([Q1]), "depth" : 25 * mm});
        }
        {
            var Q0;
            Q0=makeQuery(id+"F3.boolean.opBoolean","COPY",EDGE,{"derivedFrom":makeQuery(id+"F3.opExtrude","CAP_EDGE",EDGE,{"disambiguationData":[OSD([sQuery(id+"F0.wireOp",EDGE,"E25.6")])],"isStart":false})});
            var Q1;
            Q1=makeQuery(id+"F8.boolean.opBoolean","INTERSECT",EDGE,{"derivedFrom":[makeQuery(id+"F5.opExtrude","SWEPT_FACE",FACE,{"disambiguationData":[OSD([sQuery(id+"F4.wireOp",EDGE,"E30")])]}),makeQuery(id+"F8.opExtrude","CAP_FACE",FACE,{"disambiguationData":[OSD([sQuery(id+"F7.wireOp",EDGE,"E67")])],"isStart":false})]});
            var Q2;
            Q2=makeQuery(id+"F8.boolean.opBoolean","INTERSECT",EDGE,{"disambiguationData":[OD(1.0)],"derivedFrom":[makeQuery(id+"F5.opExtrude","SWEPT_FACE",FACE,{"disambiguationData":[OSD([sQuery(id+"F4.wireOp",EDGE,"E30")])]}),makeQuery(id+"F8.opExtrude","SWEPT_FACE",FACE,{"disambiguationData":[OSD([sQuery(id+"F7.wireOp",EDGE,"E67")])]})]});
            var Q3;
            {var subQ0=sQuery(id+"F4.wireOp",EDGE,"E30");Q3=makeQuery(id+"F8.boolean.opBoolean","SPLIT",EDGE,{"disambiguationData":[TD([makeQuery(id+"F5.opExtrude","SWEPT_FACE",FACE,{"disambiguationData":[OSD([sQuery(id+"F4.wireOp",EDGE,"E35.filletArc")])]})])],"derivedFrom":makeQuery(id+"F5.opExtrude","CAP_EDGE",EDGE,{"disambiguationData":[OSD([subQ0])],"isStart":false})});}
            var Q4;
            {var subQ0=sQuery(id+"F0.wireOp",EDGE,"E25.7");var subQ1=sQuery(id+"F0.wireOp",EDGE,"E25.1");var subQ2=sQuery(id+"F0.wireOp",EDGE,"E25.6");var subQ3=sQuery(id+"F0.wireOp",EDGE,"E25.5");var subQ4=sQuery(id+"F0.wireOp",EDGE,"E25.4");var subQ5=sQuery(id+"F0.wireOp",EDGE,"E25.0");var subQ6=sQuery(id+"F0.wireOp",EDGE,"E25.2");var subQ7=sQuery(id+"F0.wireOp",EDGE,"E25.3");Q4=makeQuery(id+"F8.boolean.opBoolean","INTERSECT",EDGE,{"derivedFrom":[makeQuery(id+"F5.boolean.opBoolean","SPLIT",FACE,{"disambiguationData":[TD([makeQuery(id+"F2.opExtrude","SWEPT_FACE",FACE,{"disambiguationData":[OSD([subQ5])]})])],"derivedFrom":makeQuery(id+"F3.boolean.opBoolean","COPY",FACE,{"derivedFrom":makeQuery(id+"F3.opExtrude","CAP_FACE",FACE,{"disambiguationData":[OSD([subQ5,subQ1,subQ6,subQ7,subQ4,subQ3,subQ2,subQ0])],"isStart":false})})}),makeQuery(id+"F8.opExtrude","SWEPT_FACE",FACE,{"disambiguationData":[OSD([sQuery(id+"F7.wireOp",EDGE,"E67")])]})]});}
            var Q5;
            Q5=makeQuery(id+"F8.boolean.opBoolean","INTERSECT",EDGE,{"disambiguationData":[OD(0.0)],"derivedFrom":[makeQuery(id+"F5.opExtrude","SWEPT_FACE",FACE,{"disambiguationData":[OSD([sQuery(id+"F4.wireOp",EDGE,"E30")])]}),makeQuery(id+"F8.opExtrude","SWEPT_FACE",FACE,{"disambiguationData":[OSD([sQuery(id+"F7.wireOp",EDGE,"E67")])]})]});
            fillet(context, id + "F14", {"entities" : qUnion([Q0, Q1, Q2, Q3, Q4, Q5]), "radius" : 3 * mm, "tangentPropagation" : true, "allowEdgeOverflow" : false});
        }
        {
            var Q0;
            Q0=makeQuery(id+"F1.opExtrude","CAP_EDGE",EDGE,{"disambiguationData":[OSD([sQuery(id+"F0.wireOp",EDGE,"E1.bottom")])],"isStart":false});
            fillet(context, id + "F15", {"entities" : qUnion([Q0]), "radius" : 2 * mm, "tangentPropagation" : true, "allowEdgeOverflow" : false});
        }
        {
            var Q0;
            {var subQ0=sQuery(id+"F0.wireOp",EDGE,"E22.filletArc");var subQ1=sQuery(id+"F0.wireOp",EDGE,"E7");var subQ2=sQuery(id+"F0.wireOp",EDGE,"E6");var subQ3=sQuery(id+"F0.wireOp",EDGE,"E5");var subQ4=sQuery(id+"F0.wireOp",EDGE,"E4");var subQ5=sQuery(id+"F0.wireOp",EDGE,"E1.bottom");var subQ6=sQuery(id+"F0.wireOp",EDGE,"E21.filletArc");var subQ7=sQuery(id+"F0.wireOp",EDGE,"E1.top");var subQ8=sQuery(id+"F0.wireOp",EDGE,"E1.left");var subQ9=sQuery(id+"F0.wireOp",EDGE,"E1.right");var subQ10=sQuery(id+"F0.wireOp",EDGE,"E23.filletArc");var subQ11=sQuery(id+"F0.wireOp",EDGE,"E24.filletArc");Q0=makeQuery(id+"F2.boolean.opBoolean","SPLIT",FACE,{"disambiguationData":[TD([makeQuery(id+"F1.opExtrude","SWEPT_FACE",FACE,{"disambiguationData":[OSD([subQ5])]})])],"derivedFrom":makeQuery(id+"F1.opExtrude","CAP_FACE",FACE,{"disambiguationData":[OSD([subQ5,subQ7,subQ8,subQ9,subQ4,subQ3,subQ2,subQ1,subQ6,subQ0,subQ10,subQ11])],"isStart":true})});}
            var sketch = newSketch(context, id + "F16", { "sketchPlane" : qUnion([Q0])});
            skPoint(sketch, "E79.startSnap0", {"position": v(0, 74.25) * mm});
            skCircle(sketch, "E80", {"center": v(0, 104.25) * mm, "radius": 6 * mm});
            skLineSegment(sketch, "E81", {"start": v(-33, 74.25) * mm, "end": v(-15, 92.25) * mm});
            skLineSegment(sketch, "E82", {"start": v(-15, 92.25) * mm, "end": v(-15, 104.25) * mm});
            skArc(sketch, "E83", {"start": v(15, 104.25) * mm, "mid": v(0, 119.25) * mm, "end": v(-15, 104.25) * mm});
            skLineSegment(sketch, "E84", {"start": v(15, 104.25) * mm, "end": v(15, 92.25) * mm});
            skLineSegment(sketch, "E85", {"start": v(15, 92.25) * mm, "end": v(33, 74.25) * mm});
            skLineSegment(sketch, "E86.MirrorCS", {"start": v(-33, -74.25) * mm, "end": v(-15, -92.25) * mm});
            skLineSegment(sketch, "E87.MirrorCS", {"start": v(-15, -92.25) * mm, "end": v(-15, -104.25) * mm});
            skArc(sketch, "E88.MirrorCS", {"start": v(15, -104.25) * mm, "mid": v(0, -119.25) * mm, "end": v(-15, -104.25) * mm});
            skCircle(sketch, "E89.MirrorC", {"center": v(0, -104.25) * mm, "radius": 6 * mm});
            skLineSegment(sketch, "E90.MirrorCS", {"start": v(0, -74.25) * mm, "end": v(0, -104.25) * mm, "construction": true});
            skLineSegment(sketch, "E91.MirrorCS", {"start": v(15, -92.25) * mm, "end": v(33, -74.25) * mm});
            skLineSegment(sketch, "E92.MirrorCS", {"start": v(15, -104.25) * mm, "end": v(15, -92.25) * mm});
            skLineSegment(sketch, "E93", {"start": v(0, 104.25) * mm, "end": v(0, 74.25) * mm, "construction": true});
            skSolve(sketch);
        }
        {
            var Q0;
            Q0=makeQuery(id+"F16.imprint","IMPRINT",FACE,{"disambiguationData":[TD([[makeQuery(id+"F16.imprint","IMPRINT",EDGE,{"derivedFrom":sQuery(id+"F16.wireOp",EDGE,"E80")}),-1.0]])]});
            var Q1;
            Q1=makeQuery(id+"F16.imprint","IMPRINT",FACE,{"disambiguationData":[TD([[makeQuery(id+"F16.imprint","IMPRINT",EDGE,{"derivedFrom":makeQuery(id+"F1.opExtrude","CAP_EDGE",EDGE,{"disambiguationData":[OSD([sQuery(id+"F0.wireOp",EDGE,"E1.left")])],"isStart":true})}),-1.0]])]});
            var Q2;
            {var subQ0=sQuery(id+"F16.wireOp",EDGE,"E86.MirrorCS");Q2=makeQuery(id+"F16.imprint","IMPRINT",FACE,{"disambiguationData":[TD([[makeQuery(id+"F16.imprint","IMPRINT",EDGE,{"derivedFrom":subQ0}),1.0]])]});}
            var Q3;
            Q3=makeQuery(id+"F2.opExtrude","CAP_FACE",FACE,{"disambiguationData":[OSD([sQuery(id+"F0.wireOp",EDGE,"E12"),sQuery(id+"F0.wireOp",EDGE,"E13"),sQuery(id+"F0.wireOp",EDGE,"E14"),sQuery(id+"F0.wireOp",EDGE,"E15"),sQuery(id+"F0.wireOp",EDGE,"E17.filletArc"),sQuery(id+"F0.wireOp",EDGE,"E18.filletArc"),sQuery(id+"F0.wireOp",EDGE,"E19.filletArc"),sQuery(id+"F0.wireOp",EDGE,"E20.filletArc"),sQuery(id+"F0.wireOp",EDGE,"E25.0"),sQuery(id+"F0.wireOp",EDGE,"E25.1"),sQuery(id+"F0.wireOp",EDGE,"E25.2"),sQuery(id+"F0.wireOp",EDGE,"E25.3"),sQuery(id+"F0.wireOp",EDGE,"E25.4"),sQuery(id+"F0.wireOp",EDGE,"E25.5"),sQuery(id+"F0.wireOp",EDGE,"E25.6"),sQuery(id+"F0.wireOp",EDGE,"E25.7")])],"isStart":false});
            extrude(context, id + "F17", {"entities" : qUnion([Q0, Q1, Q2]), "endBound" : BoundingType.UP_TO_SURFACE, "endBoundEntityFace" : qUnion([Q3]), "depth" : 25 * mm});
        }
    });
